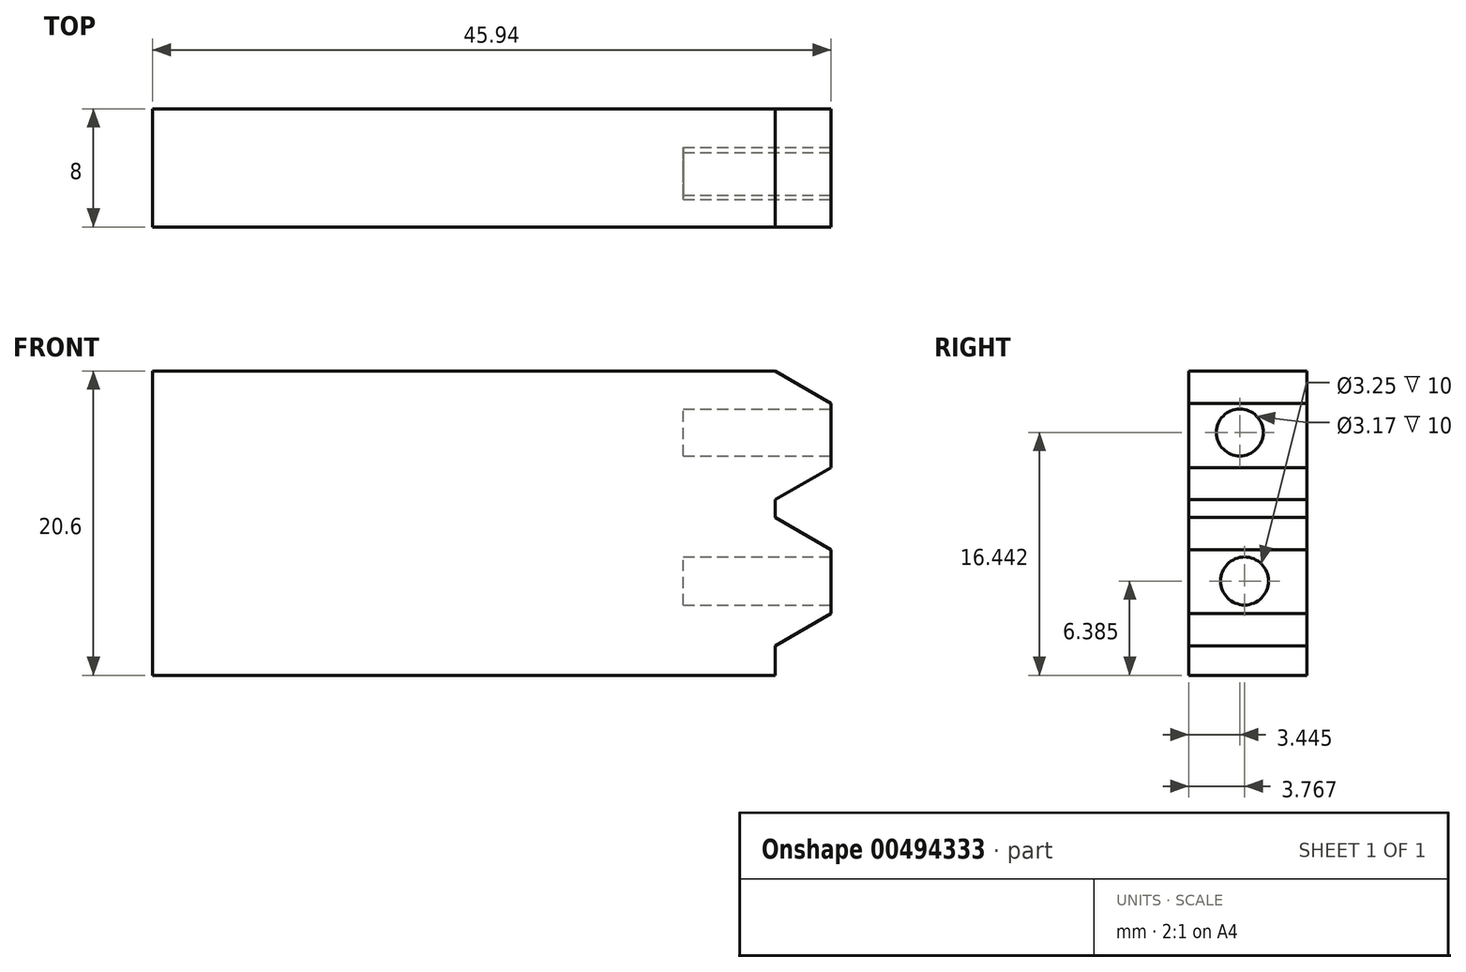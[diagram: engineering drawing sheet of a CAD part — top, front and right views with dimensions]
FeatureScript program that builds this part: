
annotation { "Feature Type Name" : "Feature", "Feature Type Description" : "" }
export const myFeature = defineFeature(function(context is Context, id is Id, definition is map)
    precondition{}
    {
        {
            var Q0;
            Q0=qCreatedBy(makeId("Front.planeOp"),FACE);
            var sketch = newSketch(context, id + "F0", { "sketchPlane" : qUnion([Q0])});
            skLineSegment(sketch, "E0.bottom", {"start": v(-42.18, 29.31) * mm, "end": v(0, 29.31) * mm});
            skLineSegment(sketch, "E0.top", {"start": v(-42.18, 8.71) * mm, "end": v(0, 8.71) * mm});
            skLineSegment(sketch, "E0.left", {"start": v(-42.18, 29.31) * mm, "end": v(-42.18, 8.71) * mm});
            skLineSegment(sketch, "E0.right", {"start": v(0, 29.31) * mm, "end": v(0, 8.71) * mm});
            skSolve(sketch);
        }
        {
            var Q0;
            Q0=makeQuery(id+"F0.imprint","IMPRINT",FACE,{"disambiguationData":[TD([[makeQuery(id+"F0.imprint","IMPRINT",EDGE,{"derivedFrom":sQuery(id+"F0.wireOp",EDGE,"E0.bottom")}),-1.0]])]});
            var sketch = newSketch(context, id + "F1", { "sketchPlane" : qUnion([Q0])});
            skCircle(sketch, "E1.cCircle", {"center": v(0, 24.95) * mm, "radius": 3.76 * mm, "construction": true});
            skLineSegment(sketch, "E1.0", {"start": v(-3.76, 22.78) * mm, "end": v(-3.76, 27.13) * mm});
            skLineSegment(sketch, "E1.1", {"start": v(-3.76, 27.13) * mm, "end": v(0, 29.3) * mm});
            skLineSegment(sketch, "E1.2", {"start": v(0, 29.3) * mm, "end": v(3.76, 27.13) * mm});
            skLineSegment(sketch, "E1.3", {"start": v(3.76, 27.13) * mm, "end": v(3.76, 22.78) * mm});
            skLineSegment(sketch, "E1.4", {"start": v(3.76, 22.78) * mm, "end": v(0, 20.6) * mm});
            skLineSegment(sketch, "E1.5", {"start": v(0, 20.6) * mm, "end": v(-3.76, 22.78) * mm});
            skPoint(sketch, "E1.0.midPoint", {"position": v(-3.76, 24.95) * mm});
            skCircle(sketch, "E2.cCircle", {"center": v(0, 15.05) * mm, "radius": 3.76 * mm, "construction": true});
            skLineSegment(sketch, "E2.0", {"start": v(3.76, 17.22) * mm, "end": v(3.76, 12.88) * mm});
            skLineSegment(sketch, "E2.1", {"start": v(3.76, 12.88) * mm, "end": v(0, 10.7) * mm});
            skLineSegment(sketch, "E2.2", {"start": v(0, 10.7) * mm, "end": v(-3.76, 12.88) * mm});
            skLineSegment(sketch, "E2.3", {"start": v(-3.76, 12.88) * mm, "end": v(-3.76, 17.22) * mm});
            skLineSegment(sketch, "E2.4", {"start": v(-3.76, 17.22) * mm, "end": v(0, 19.4) * mm});
            skLineSegment(sketch, "E2.5", {"start": v(0, 19.4) * mm, "end": v(3.76, 17.22) * mm});
            skPoint(sketch, "E2.0.midPoint", {"position": v(3.76, 15.05) * mm});
            skSolve(sketch);
        }
        {
            var Q0;
            Q0 = qSketchRegion(id + "F0", true);
            extrude(context, id + "F2", {"entities" : qUnion([Q0]), "depth" : 8 * mm});
        }
        {
            var Q0;
            Q0 = qSketchRegion(id + "F1", true);
            extrude(context, id + "F3", {"entities" : qUnion([Q0]), "operationType" : NewBodyOperationType.ADD, "depth" : 8 * mm});
        }
        {
            var Q0;
            Q0=makeQuery(id+"F3.opExtrude","SWEPT_FACE",FACE,{"disambiguationData":[OSD([sQuery(id+"F1.wireOp",EDGE,"E2.0")])]});
            var sketch = newSketch(context, id + "F4", { "sketchPlane" : qUnion([Q0])});
            skCircle(sketch, "E3", {"center": v(-4.23, 15.1) * mm, "radius": 1.62 * mm});
            skSolve(sketch);
        }
        {
            var Q0;
            Q0=makeQuery(id+"F4.imprint","IMPRINT",FACE,{"disambiguationData":[TD([[makeQuery(id+"F4.imprint","IMPRINT",EDGE,{"derivedFrom":sQuery(id+"F4.wireOp",EDGE,"E3")}),1.0]])]});
            extrude(context, id + "F5", {"entities" : qUnion([Q0]), "operationType" : NewBodyOperationType.REMOVE, "oppositeDirection" : true, "depth" : 10 * mm});
        }
        {
            var Q0;
            Q0=makeQuery(id+"F3.opExtrude","SWEPT_FACE",FACE,{"disambiguationData":[OSD([sQuery(id+"F1.wireOp",EDGE,"E1.3")])]});
            var sketch = newSketch(context, id + "F6", { "sketchPlane" : qUnion([Q0])});
            skCircle(sketch, "E4", {"center": v(-4.56, 25.15) * mm, "radius": 1.58 * mm});
            skSolve(sketch);
        }
        {
            var Q0;
            Q0=makeQuery(id+"F6.imprint","IMPRINT",FACE,{"disambiguationData":[TD([[makeQuery(id+"F6.imprint","IMPRINT",EDGE,{"derivedFrom":sQuery(id+"F6.wireOp",EDGE,"E4")}),1.0]])]});
            var Q1;
            Q1=sQuery(id+"F6.wireOp",EDGE,"E4");
            extrude(context, id + "F7", {"entities" : qUnion([Q0]), "operationType" : NewBodyOperationType.REMOVE, "surfaceEntities" : qUnion([Q1]), "oppositeDirection" : true, "depth" : 10 * mm});
        }
        {
            var Q0;
            Q0=makeQuery(id+"F3.boolean.opBoolean","MERGE",FACE,{"derivedFrom":[makeQuery(id+"F2.opExtrude","CAP_FACE",FACE,{"disambiguationData":[OSD([sQuery(id+"F0.wireOp",EDGE,"E0.bottom"),sQuery(id+"F0.wireOp",EDGE,"E0.top"),sQuery(id+"F0.wireOp",EDGE,"E0.left"),sQuery(id+"F0.wireOp",EDGE,"E0.right")])],"isStart":false}),makeQuery(id+"F3.opExtrude","CAP_FACE",FACE,{"disambiguationData":[OSD([sQuery(id+"F1.wireOp",EDGE,"E1.0"),sQuery(id+"F1.wireOp",EDGE,"E1.1"),sQuery(id+"F1.wireOp",EDGE,"E1.2"),sQuery(id+"F1.wireOp",EDGE,"E1.3"),sQuery(id+"F1.wireOp",EDGE,"E1.4"),sQuery(id+"F1.wireOp",EDGE,"E1.5")])],"isStart":false}),makeQuery(id+"F3.opExtrude","CAP_FACE",FACE,{"disambiguationData":[OSD([sQuery(id+"F1.wireOp",EDGE,"E2.0"),sQuery(id+"F1.wireOp",EDGE,"E2.1"),sQuery(id+"F1.wireOp",EDGE,"E2.2"),sQuery(id+"F1.wireOp",EDGE,"E2.3"),sQuery(id+"F1.wireOp",EDGE,"E2.4"),sQuery(id+"F1.wireOp",EDGE,"E2.5")])],"isStart":false})]});
            var sketch = newSketch(context, id + "F8", { "sketchPlane" : qUnion([Q0])});
            skLineSegment(sketch, "E5", {"start": v(-42.18, 27.77) * mm, "end": v(0, 27.77) * mm});
            skLineSegment(sketch, "E6", {"start": v(-42.18, 25.81) * mm, "end": v(0, 25.81) * mm});
            skLineSegment(sketch, "E7", {"start": v(-42.18, 24.27) * mm, "end": v(0, 24.27) * mm});
            skLineSegment(sketch, "E8", {"start": v(-42.18, 22.73) * mm, "end": v(0, 22.73) * mm});
            skLineSegment(sketch, "E9", {"start": v(-42.18, 20.6) * mm, "end": v(0, 20.6) * mm});
            skSolve(sketch);
        }
    });
